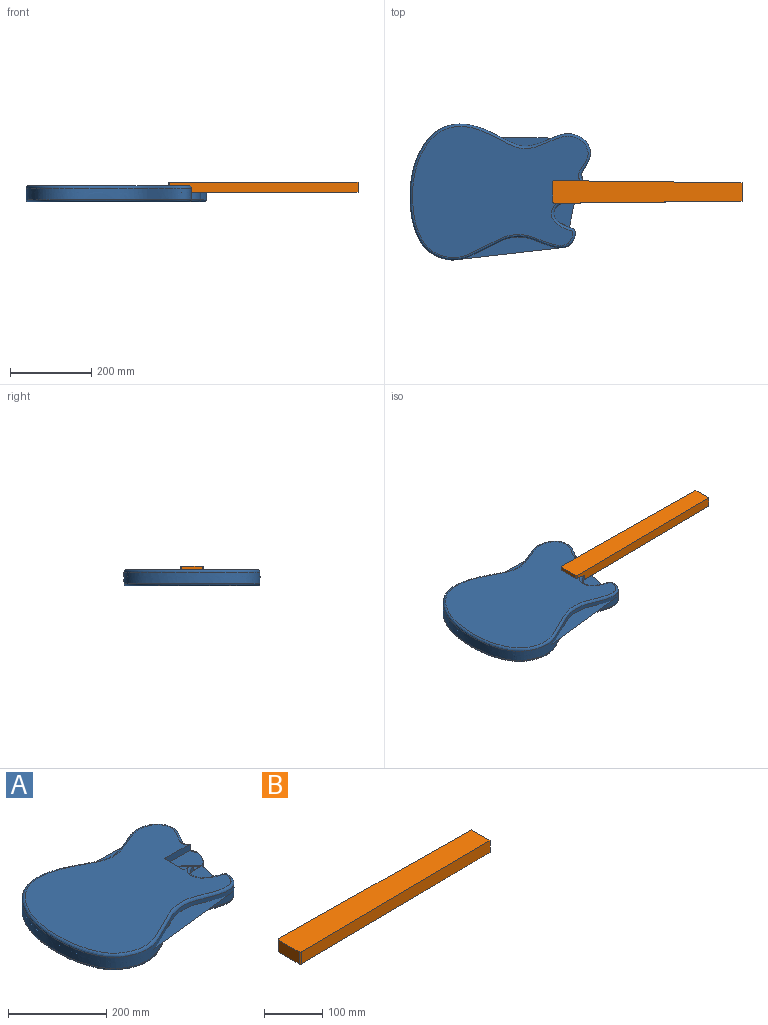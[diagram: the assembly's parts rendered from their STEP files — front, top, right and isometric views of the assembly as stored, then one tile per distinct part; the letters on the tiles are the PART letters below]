
ASSEMBLY  parts=2 mates=1
PART A: 13 faces, bbox 1257.3x1147.5x853.1 mm
  f0: plane 50x16mm, normal (1,0,0), area 800mm2, adj f1,f6,f9,f10
  f1: plane 432.25x322.73mm, normal (0,0,1), area 98019.3mm2, adj f0,f4,f5,f9,f10,f12
  f2: extruded ~442.85x327.41mm, area 57565.2mm2, adj f5,f6,f7,f8,f11,f12
  f3: plane 432.25x322.73mm, normal (0,0,-1), area 102312.4mm2, adj f11
  f4: plane 25.33x16mm, normal (-0.01,1,0), area 374.2mm2, adj f1,f6,f7,f10,f12
  f5: plane 72.36x16mm, normal (-0.01,-1,0), area 1148.5mm2, adj f1,f2,f6,f9,f12
  f6: plane 891.78x869.05mm, normal (0,0,1), area 4002.8mm2, adj f0,f2,f4,f5,f8,f9,f10
  f7: plane 31.91x0.38mm, normal (0.99,-0.13,0), area 9.8mm2, adj f2,f4,f8,f11,f12
  f8: plane 827.89x826.03mm, normal (0.01,-1,0), area 451mm2, adj f2,f6,f7,f11
  f9: cylinder r=3mm len=16mm, axis (0,0,-1), area 74.9mm2, adj f0,f1,f5,f6
  f10: cylinder r=3mm len=16mm, axis (0,0,-1), area 74.9mm2, adj f0,f1,f4,f6
  f11: bspline ~441.42x334.2mm, area 13305.3mm2, adj f2,f3,f7,f8
  f12: bspline ~443.95x334.36mm, area 12452.8mm2, adj f1,f2,f4,f5,f7
PART B: 8 faces, bbox 465.7x55.9x25 mm
  f0: plane 49.93x25mm, normal (-1,0,0), area 1248.2mm2, adj f2,f3,f6,f7
  f1: plane 45x25mm, normal (1,0,0), area 1125mm2, adj f2,f3,f4,f5
  f2: plane 465.68x55.93mm, normal (0,0,1), area 23512.6mm2, adj f0,f1,f4,f5,f6,f7
  f3: plane 465.68x55.93mm, normal (0,0,-1), area 23512.6mm2, adj f0,f1,f4,f5,f6,f7
  f4: plane 462.65x25mm, normal (0.01,-1,0), area 11567mm2, adj f1,f2,f3,f6
  f5: plane 462.65x25mm, normal (0.01,1,0), area 11567mm2, adj f1,f2,f3,f7
  f6: cylinder r=3mm len=25mm, axis (0,0,-1), area 118.7mm2, adj f0,f2,f3,f4
  f7: cylinder r=3mm len=25mm, axis (0,0,-1), area 118.7mm2, adj f0,f2,f3,f5
PLACE A t=(-112.91,21.02,120.5)mm
PLACE B t=(17.78,-6.98,144.5)mm
MATE fastened A.f0 <-> B.f0  axis (1,0,0) through (17.78,21.02,144.5)mm
